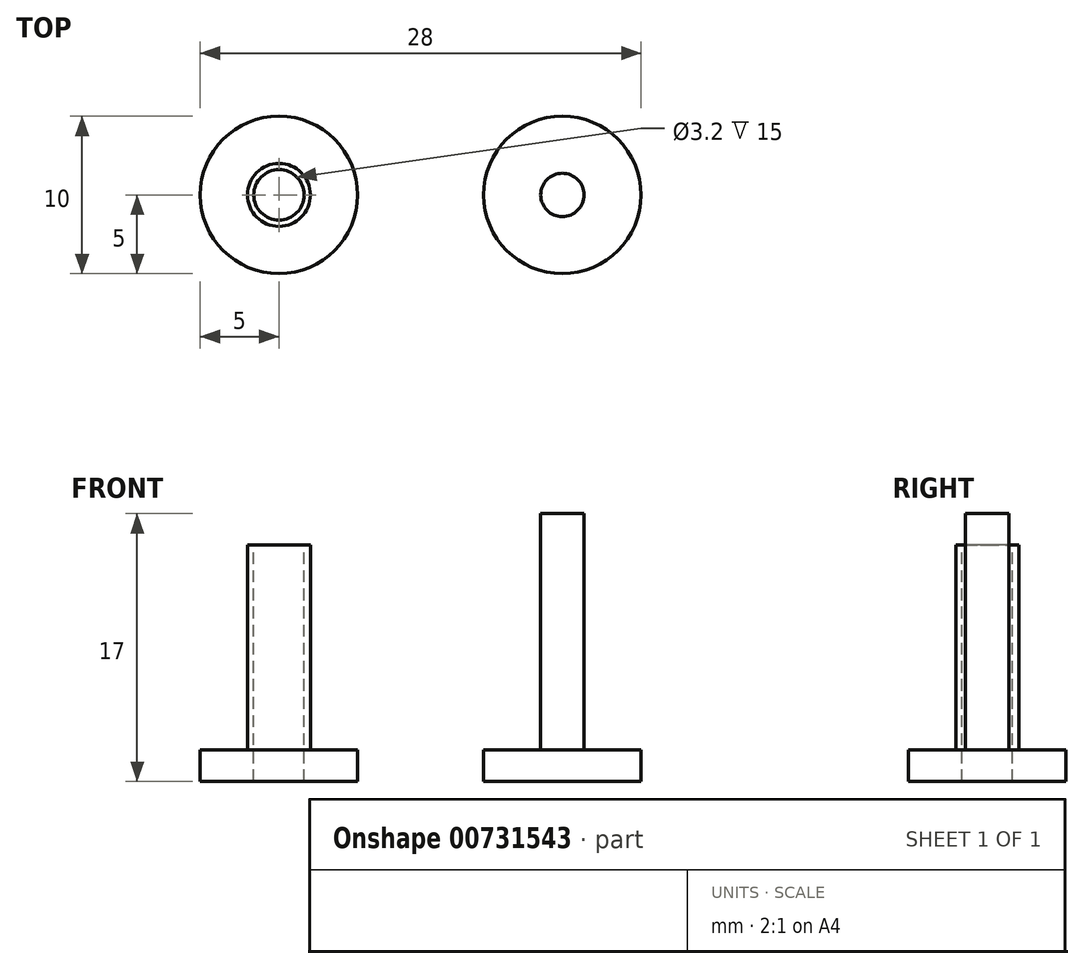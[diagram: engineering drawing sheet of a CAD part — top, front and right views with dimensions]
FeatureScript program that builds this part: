
annotation { "Feature Type Name" : "Feature", "Feature Type Description" : "" }
export const myFeature = defineFeature(function(context is Context, id is Id, definition is map)
    precondition{}
    {
        {
            var Q0;
            Q0=qCreatedBy(makeId("Top.planeOp"),FACE);
            var sketch = newSketch(context, id + "F0", { "sketchPlane" : qUnion([Q0])});
            skCircle(sketch, "E0", {"center": v(0, 0) * mm, "radius": 5 * mm});
            skSolve(sketch);
        }
        {
            var Q0;
            Q0 = qSketchRegion(id + "F0", true);
            extrude(context, id + "F1", {"entities" : qUnion([Q0]), "depth" : 2 * mm, "offsetDistance" : 25 * mm});
        }
        {
            var Q0;
            Q0=makeQuery(id+"F1.opExtrude","CAP_FACE",FACE,{"disambiguationData":[OSD([sQuery(id+"F0.wireOp",EDGE,"E0")])],"isStart":false});
            var sketch = newSketch(context, id + "F2", { "sketchPlane" : qUnion([Q0])});
            skCircle(sketch, "E1", {"center": v(0, 0) * mm, "radius": 2 * mm});
            skSolve(sketch);
        }
        {
            var Q0;
            Q0=makeQuery(id+"F2.imprint","IMPRINT",FACE,{"disambiguationData":[TD([[makeQuery(id+"F2.imprint","IMPRINT",EDGE,{"derivedFrom":sQuery(id+"F2.wireOp",EDGE,"E1")}),1.0]])]});
            extrude(context, id + "F3", {"entities" : qUnion([Q0]), "operationType" : NewBodyOperationType.ADD, "depth" : 13 * mm, "offsetDistance" : 25 * mm});
        }
        {
            var Q0;
            Q0=makeQuery(id+"F3.opExtrude","CAP_FACE",FACE,{"disambiguationData":[OSD([sQuery(id+"F2.wireOp",EDGE,"E1")])],"isStart":false});
            var sketch = newSketch(context, id + "F4", { "sketchPlane" : qUnion([Q0])});
            skCircle(sketch, "E2", {"center": v(0, 0) * mm, "radius": 1.6 * mm});
            skSolve(sketch);
        }
        {
            var Q0;
            Q0=makeQuery(id+"F4.imprint","IMPRINT",FACE,{"disambiguationData":[TD([[makeQuery(id+"F4.imprint","IMPRINT",EDGE,{"derivedFrom":sQuery(id+"F4.wireOp",EDGE,"E2")}),1.0]])]});
            extrude(context, id + "F5", {"entities" : qUnion([Q0]), "operationType" : NewBodyOperationType.REMOVE, "endBound" : BoundingType.THROUGH_ALL, "oppositeDirection" : true, "depth" : 25 * mm, "offsetDistance" : 25 * mm});
        }
        {
            var Q0;
            Q0=qCreatedBy(makeId("Top.planeOp"),FACE);
            var sketch = newSketch(context, id + "F6", { "sketchPlane" : qUnion([Q0])});
            skCircle(sketch, "E3", {"center": v(18, 0) * mm, "radius": 5 * mm});
            skSolve(sketch);
        }
        {
            var Q0;
            Q0=makeQuery(id+"F6.imprint","IMPRINT",FACE,{"disambiguationData":[TD([[makeQuery(id+"F6.imprint","IMPRINT",EDGE,{"derivedFrom":sQuery(id+"F6.wireOp",EDGE,"E3")}),1.0]])]});
            extrude(context, id + "F7", {"entities" : qUnion([Q0]), "depth" : 2 * mm, "offsetDistance" : 25 * mm});
        }
        {
            var Q0;
            Q0=makeQuery(id+"F7.opExtrude","CAP_FACE",FACE,{"disambiguationData":[OSD([sQuery(id+"F6.wireOp",EDGE,"E3")])],"isStart":false});
            var sketch = newSketch(context, id + "F8", { "sketchPlane" : qUnion([Q0])});
            skCircle(sketch, "E4", {"center": v(18, 0) * mm, "radius": 1.38 * mm});
            skSolve(sketch);
        }
        {
            var Q0;
            Q0=makeQuery(id+"F8.imprint","IMPRINT",FACE,{"disambiguationData":[TD([[makeQuery(id+"F8.imprint","IMPRINT",EDGE,{"derivedFrom":sQuery(id+"F8.wireOp",EDGE,"E4")}),1.0]])]});
            extrude(context, id + "F9", {"entities" : qUnion([Q0]), "operationType" : NewBodyOperationType.ADD, "depth" : 15 * mm, "offsetDistance" : 25 * mm});
        }
    });
